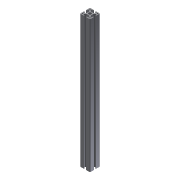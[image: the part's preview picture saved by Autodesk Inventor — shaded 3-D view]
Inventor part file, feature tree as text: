
AUTODESK INVENTOR PART (.ipt)
format: ipt  version: 2016 (Build 200138000, 138)  size: 182,784 bytes
history: native  units: mm
features: other x42, sketch x5, hole x4, extrude x1
ambient origin geometry x8: Origin, YZ Plane, XZ Plane, XY Plane, X Axis, Y Axis, Z Axis, Center Point
bodies: Solid1 (feature_tree)
feature tree (52):
  extrude  "Extrusion1"  [1 undecoded]
  hole  "Drilling 1"  [1 undecoded]
  hole  "Drilling 2"  [1 undecoded]
  hole  "Drilling 3"  [1 undecoded]
  hole  "Drilling 4"  [1 undecoded]
  other  "side_4d_XY"
  other  "side_4d_YZ"
  other  "side_4d_ZX"
  other  "side_4d_X"
  other  "side_4d_Y"
  other  "side_4d_Z"
  other  "side_4d_Center"
  other  "side_1a_XY"
  other  "side_1a_YZ"
  other  "side_1a_ZX"
  other  "side_1a_X"
  other  "side_1a_Y"
  other  "side_1a_Z"
  other  "side_1a_Center"
  other  "side_2b_XY"
  other  "side_2b_YZ"
  other  "side_2b_ZX"
  other  "side_2b_X"
  other  "side_2b_Y"
  other  "side_2b_Z"
  other  "side_2b_Center"
  other  "side_3c_XY"
  other  "side_3c_YZ"
  other  "side_3c_ZX"
  other  "side_3c_X"
  other  "side_3c_Y"
  other  "side_3c_Z"
  other  "side_3c_Center"
  other  "end_XY"
  other  "end_YZ"
  other  "end_ZX"
  other  "end_X"
  other  "end_Y"
  other  "end_Z"
  other  "end_Center"
  other  "start_XY"
  other  "start_YZ"
  other  "start_ZX"
  other  "start_X"
  other  "start_Y"
  other  "start_Z"
  other  "start_Center"
  sketch  "Skizze_1"  dims[d0=529.8mm d1=0.0mm]
  sketch  "Sketch2"  dims[d2=5.0mm d3=6.0mm d4=4.0mm d5=2.0mm d6=90.0deg d7=6000.0mm d8=0.0mm]
  sketch  "Sketch3"  dims[d9=5.0mm d10=6.0mm d11=4.0mm d12=2.0mm d13=90.0deg d14=6000.0mm d15=0.0mm]
  sketch  "Sketch4"  dims[d16=5.0mm d17=6.0mm d18=4.0mm d19=2.0mm d20=90.0deg d21=6000.0mm d22=0.0mm]
  sketch  "Sketch5"  dims[d23=5.0mm d24=6.0mm d25=4.0mm d26=2.0mm d27=90.0deg d28=6000.0mm d29=0.0mm]
note: 5 required parameter values undecoded (feature->parameter linkage not recoverable at this tier; creation-order binding heuristic only, values carry confidence <= 0.55)
